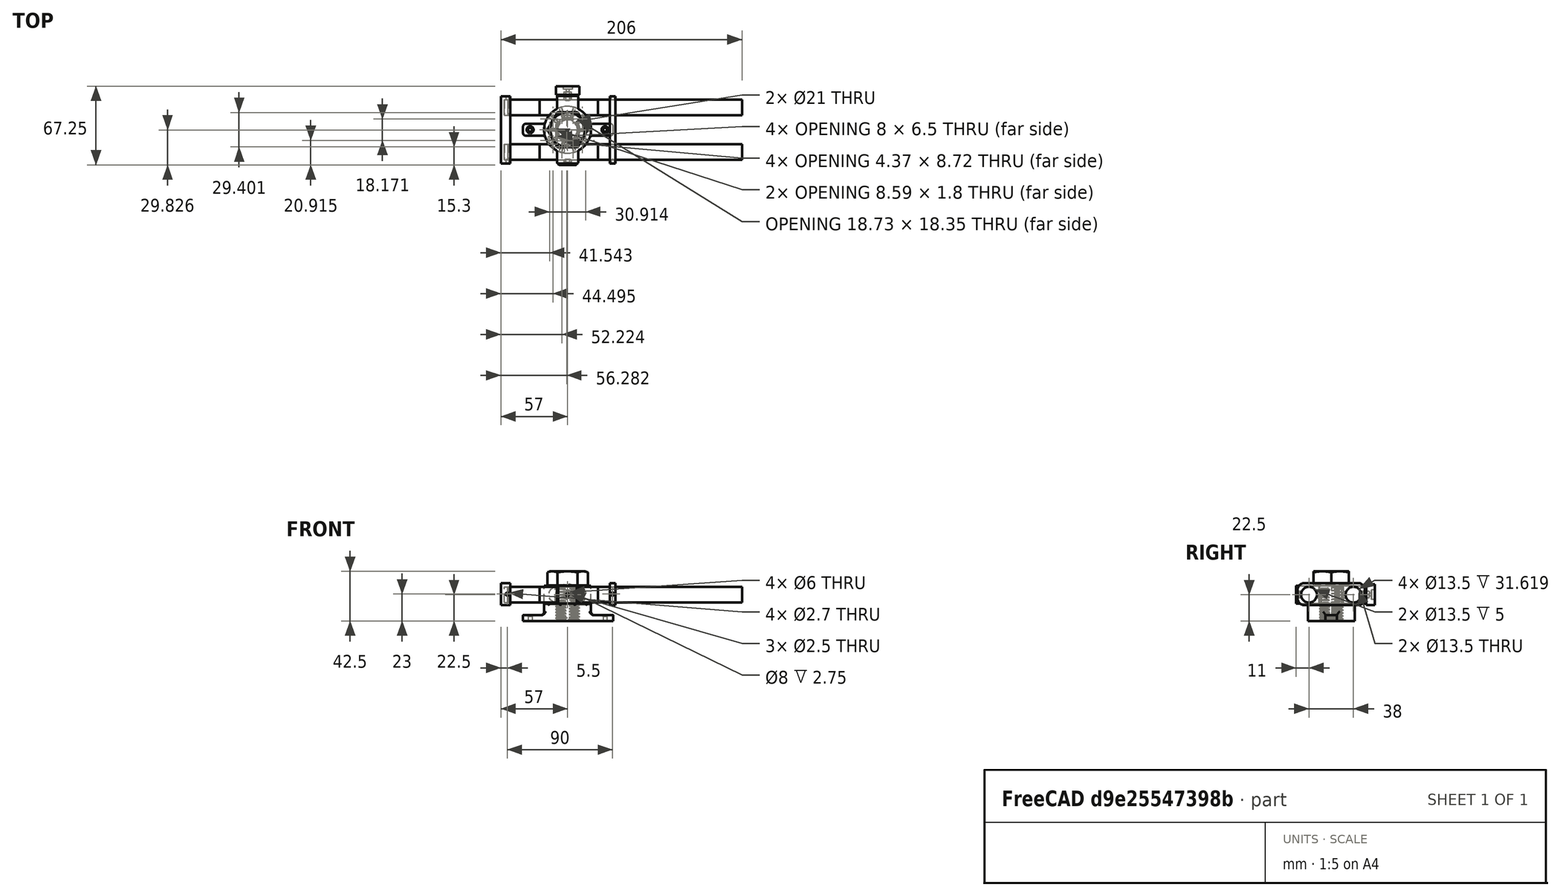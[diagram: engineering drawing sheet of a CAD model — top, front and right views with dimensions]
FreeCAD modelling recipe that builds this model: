
FCSTD DOCUMENT  (FreeCAD 0.18R4 (GitTag))
Label: soporte_microfono
License: All rights reserved
LicenseURL: http://en.wikipedia.org/wiki/All_rights_reserved
objects: Part::Cylinder×31, Part::Cut×25, Part::Box×11, Part::Fillet×11, Part::MultiFuse×9, Mesh::Feature×7, Part::FeaturePython×5, App::DocumentObjectGroup×4, Part::Prism×3, Sketcher::SketchObject×2, PartDesign::FeatureBase×2, PartDesign::Hole×2, PartDesign::Body×2, PartDesign::Mirrored×1, PartDesign::MultiTransform×1
note: 107 computed .brp shape members not serialized (recipe doc carries the construction recipe); baked Part::Feature solids carry a one-line shape summary decoded from their .brp

FEATURE [Part::Cylinder] Cylinder
  Angle = 360
  AttacherType = Attacher::AttachEngine3D
  Height = 15
  Radius = 20
FEATURE [Part::Cylinder] Cylinder001
  Angle = 360
  AttacherType = Attacher::AttachEngine3D
  Height = 22
  Placement = pos=(0,0,15) rot=(0,1,0;1.5708rad)
  Radius = 1.1
FEATURE [Part::FeaturePython] Array  # Draft array (typed FeaturePython)
  Angle = 360
  ArrayType = 1
  Axis = (0,0,1)
  Base = -> Cylinder001
  Center = (0,0,0)
  Fuse = false
  IntervalAxis = (0,0,0)
  IntervalX = (1,0,0)
  IntervalY = (0,1,0)
  IntervalZ = (0,0,1)
  NumberPolar = 10
  NumberX = 2
  NumberY = 2
  NumberZ = 1
FEATURE [Part::Cylinder] Cylinder002
  Angle = 360
  AttacherType = Attacher::AttachEngine3D
  Height = 19.75
  Placement = pos=(0,0,15) rot=(0,1,0;1.5708rad)
  Radius = 0.9
FEATURE [Part::FeaturePython] Array001  # Draft array (typed FeaturePython)
  Angle = 360
  ArrayType = 1
  Axis = (0,0,1)
  Base = -> Cylinder002
  Center = (0,0,0)
  Fuse = false
  IntervalAxis = (0,0,0)
  IntervalX = (1,0,0)
  IntervalY = (0,1,0)
  IntervalZ = (0,0,1)
  NumberPolar = 10
  NumberX = 2
  NumberY = 2
  NumberZ = 1
FEATURE [Part::Cylinder] Cylinder003
  Angle = 360
  AttacherType = Attacher::AttachEngine3D
  Height = 23
  Radius = 11
FEATURE [Part::Cylinder] Cylinder004
  Angle = 360
  AttacherType = Attacher::AttachEngine3D
  Height = 23
  Radius = 11.2
FEATURE [Part::Cut] Cut001
  Base = -> Array
  Refine = true
  Tool = -> Cylinder003
FEATURE [Part::Cut] Cut002  label="aspas"
  Base = -> Array001
  Refine = true
  Tool = -> Cylinder004
FEATURE [Part::Box] Box  label="Cube"
  AttacherType = Attacher::AttachEngine3D
  Height = 5
  Length = 25
  Placement = pos=(14,-5,0) rot=(0,0,1;0rad)
  Width = 10
FEATURE [Part::Box] Box001  label="Cube001"
  AttacherType = Attacher::AttachEngine3D
  Height = 5
  Length = 25
  Placement = pos=(-38,-5,0) rot=(0,0,1;0rad)
  Width = 10
FEATURE [Part::Cylinder] Cylinder005
  Angle = 360
  AttacherType = Attacher::AttachEngine3D
  Height = 15
  Placement = pos=(0,0,15) rot=(0,0,1;0rad)
  Radius = 20
FEATURE [Part::Cylinder] Cylinder006
  Angle = 360
  AttacherType = Attacher::AttachEngine3D
  Height = 32
  Radius = 10.5
FEATURE [Part::Cut] Cut004
  Base = -> Cylinder005
  Refine = true
  Tool = -> Cylinder006
FEATURE [Part::MultiFuse] Fusion001
  Refine = true
  Shapes = -> [Cut004,Cut002]
FEATURE [Part::Cylinder] Cylinder007
  Angle = 360
  AttacherType = Attacher::AttachEngine3D
  Height = 50
  Placement = pos=(-24,19,22.5) rot=(0,1,0;1.5708rad)
  Radius = 6.75
FEATURE [Part::Box] Box002  label="Cube002"
  AttacherType = Attacher::AttachEngine3D
  Height = 15
  Length = 18
  Placement = pos=(-9,-29,15) rot=(0,0,1;0rad)
  Width = 18
FEATURE [Part::Box] Box003  label="Cube003"
  AttacherType = Attacher::AttachEngine3D
  Height = 15
  Length = 18
  Placement = pos=(-9,11,15) rot=(0,0,1;0rad)
  Width = 18
FEATURE [Part::MultiFuse] Fusion002
  Refine = true
  Shapes = -> [Fusion001,Box002,Box003]
FEATURE [Part::Cylinder] Cylinder008
  Angle = 360
  AttacherType = Attacher::AttachEngine3D
  Height = 50
  Placement = pos=(-24,-19,22.5) rot=(0,1,0;1.5708rad)
  Radius = 6.75
FEATURE [Part::Cut] Cut005
  Base = -> Fusion002
  Refine = true
  Tool = -> Cylinder008
FEATURE [Part::Cut] Cut006
  Base = -> Cut005
  Refine = true
  Tool = -> Cylinder007
FEATURE [Part::Fillet] Fillet003  label="part_soporte_inferior_estante"
  Base = -> Cut006
  Edges = 12 edges r=1: [Edge2,Edge5,Edge7,Edge19,Edge21,Edge74,Edge75,Edge76,Edge77,Edge79,Edge80,Edge83]
FEATURE [Sketcher::SketchObject] Sketch002
  ExternalGeometry = -> [Fillet003]
  MapMode = 5
  Placement = pos=(0,0,0) rot=(1,0,0;1.5708rad)
  Support = -> [XZ_Plane001]
  sketch-geometry (1):
    g0: Circle CenterX=-1e-15 CenterY=22.5 CenterZ=0 NormalX=0 NormalY=0 NormalZ=1 AngleXU=0 Radius=1.25
  constraints (2):
    c: Radius(g0) = 1.25
    c: Symmetric(g-3,g-4,g0)
FEATURE [App::DocumentObjectGroup] Group  label="sketches"
  Group = -> [Sketch002]
FEATURE [PartDesign::FeatureBase] BaseFeature001
  BaseFeature = -> Fillet003
FEATURE [PartDesign::Hole] Hole001
  BaseFeature = -> BaseFeature001
  Depth = 25
  DepthType = 1
  Diameter = 6
  DrillPoint = 1
  DrillPointAngle = 118
  HoleCutCountersinkAngle = 90
  HoleCutDepth = 0
  HoleCutDiameter = 0
  HoleCutType = 0
  ModelActualThread = false
  Profile = -> Sketch002
  Refine = true
  Tapered = false
  TaperedAngle = 90
  ThreadAngle = 0
  ThreadClass = 0
  ThreadCutOffInner = 0
  ThreadCutOffOuter = 0
  ThreadDirection = 0
  ThreadFit = 0
  ThreadPitch = 0
  ThreadSize = 0
  ThreadType = 0
  Threaded = false
FEATURE [PartDesign::Mirrored] Mirrored
  MirrorPlane = -> XZ_Plane001
  Refine = true
FEATURE [PartDesign::MultiTransform] MultiTransform
  BaseFeature = -> Hole001
  Originals = -> [Hole001]
  Refine = true
  Transformations = -> [Mirrored]
FEATURE [PartDesign::Body] Body001  label="final_soporte_inferior_estante"
  BaseFeature = -> Fillet003
  Group = -> [BaseFeature001,Sketch002,Hole001,MultiTransform,Mirrored]
  Origin = -> Origin001
  Tip = -> MultiTransform
FEATURE [Part::Cylinder] Cylinder009  label="tubo_base"
  Angle = 360
  AttacherType = Attacher::AttachEngine3D
  Height = 50
  Placement = pos=(-24,19,22.5) rot=(0,1,0;1.5708rad)
  Radius = 6.75
FEATURE [Part::FeaturePython] Screw  label="final_tornillo_soportes_estante"  # Fasteners workbench fastener (typed FeaturePython)
  Placement = pos=(0,0,30) rot=(0,0,1;0rad)
  baseObject = -> Body001 [Edge24]
  diameter = 15
  invert = false
  length = 15
  lengthCustom = 29
  matchOuter = false
  offset = 0
  thread = true
  type = 27
FEATURE [Part::FeaturePython] ScrewTap  label="M20x40.0-ScrewTap"  # Fasteners workbench fastener (typed FeaturePython)
  Placement = pos=(0,0,15) rot=(0,0,1;0rad)
  baseObject = -> Cylinder [Edge1]
  diameter = 14
  invert = false
  length = 40
  matchOuter = false
  offset = 0
  thread = true
FEATURE [Part::Cut] Cut
  Base = -> Cylinder
  Refine = true
  Tool = -> ScrewTap
FEATURE [Part::Cut] Cut003
  Base = -> Cut
  Refine = true
  Tool = -> Cut001
FEATURE [Part::MultiFuse] Fusion
  Refine = true
  Shapes = -> [Box001,Box,Cut003]
FEATURE [Part::Fillet] Fillet
  Base = -> Fusion
  Edges = 7 edges r=3: [Edge6,Edge9,Edge11,Edge42,Edge43,Edge46,Edge47]
FEATURE [Part::Fillet] Fillet001
  Base = -> Fillet
  Edges = 1 edges r=2: [Edge24]
FEATURE [Part::Fillet] Fillet002  label="final_part_soporte_superior_estante"
  Base = -> Fillet001
  Edges = 3 edges r=2: [Edge27,Edge71,Edge74]
FEATURE [PartDesign::FeatureBase] BaseFeature
  BaseFeature = -> Fillet002
FEATURE [Sketcher::SketchObject] Sketch
  MapMode = 5
  Placement = pos=(0,0,5) rot=(0,0,1;0rad)
  Support = -> [BaseFeature]
  sketch-geometry (2):
    g0: Circle CenterX=-32 CenterY=0 CenterZ=0 NormalX=0 NormalY=0 NormalZ=1 AngleXU=0 Radius=0.5
    g1: Circle CenterX=32 CenterY=0 CenterZ=0 NormalX=0 NormalY=0 NormalZ=1 AngleXU=0 Radius=0.5
  constraints (5):
    c: PointOnObject(g0,g-1)
    c: Symmetric(g0,g1,g-2)
    c: Radius(g0) = 0.5
    c: Equal(g0,g1)
    c: DistanceX(g0,g-1) = 32
FEATURE [PartDesign::Hole] Hole
  BaseFeature = -> BaseFeature
  Depth = 25
  DepthType = 1
  Diameter = 3.3
  DrillPoint = 1
  DrillPointAngle = 118
  HoleCutCountersinkAngle = 90
  HoleCutDepth = 0
  HoleCutDiameter = 6
  HoleCutType = 2
  ModelActualThread = false
  Profile = -> Sketch
  Refine = true
  Tapered = false
  TaperedAngle = 90
  ThreadAngle = 0
  ThreadClass = 0
  ThreadCutOffInner = 0
  ThreadCutOffOuter = 0
  ThreadDirection = 0
  ThreadFit = 0
  ThreadPitch = 0
  ThreadSize = 3
  ThreadType = 1
  Threaded = false
FEATURE [PartDesign::Body] Body  label="soporte_superior_estante_1"
  BaseFeature = -> Fillet002
  Group = -> [BaseFeature,Sketch,Hole]
  Origin = -> Origin
  Tip = -> Hole
FEATURE [Part::Cylinder] Cylinder010  label="Cylinder009"
  Angle = 360
  AttacherType = Attacher::AttachEngine3D
  Height = 15
  Radius = 11
FEATURE [Part::MultiFuse] Fusion003
  Refine = true
  Shapes = -> [Body,Cylinder010]
FEATURE [Part::FeaturePython] ScrewTap001  label="M20x40.0-ScrewTap001"  # Fasteners workbench fastener (typed FeaturePython)
  Placement = pos=(0,0,28.5) rot=(0,0,1;0rad)
  baseObject = -> Fusion003 [Edge143]
  diameter = 14
  invert = false
  length = 40
  matchOuter = false
  offset = 13.5
  thread = true
FEATURE [Part::Cut] Cut007  label="final_soporte_superior_estante"
  Base = -> Fusion003
  Refine = true
  Tool = -> ScrewTap001
FEATURE [Mesh::Feature] Mesh001  label="tornillo_soportes_estante (Meshed)"
FEATURE [Mesh::Feature] Mesh002  label="final_soporte_superior_estante (Meshed)"
FEATURE [Part::Cylinder] Cylinder011  label="Cylinder010"
  Angle = 360
  AttacherType = Attacher::AttachEngine3D
  Height = 50
  Placement = pos=(0,-16,22.5) rot=(1,0,0;1.5708rad)
  Radius = 1.25
FEATURE [Part::Cylinder] Cylinder012  label="Cylinder011"
  Angle = 360
  AttacherType = Attacher::AttachEngine3D
  Height = 50
  Placement = pos=(0,69,22.5) rot=(1,0,0;1.5708rad)
  Radius = 1.25
FEATURE [Part::Cut] Cut008
  Base = -> Fillet003
  Refine = true
  Tool = -> Cylinder011
FEATURE [Part::Cut] Cut009
  Base = -> Cut008
  Refine = true
  Tool = -> Cylinder012
FEATURE [Part::Prism] Prism
  AttacherType = Attacher::AttachEngine3D
  Circumradius = 3.15
  Height = 2.4
  Placement = pos=(0,28,22.5) rot=(1,0,0;1.5708rad)
  Polygon = 6
FEATURE [Part::Prism] Prism001
  AttacherType = Attacher::AttachEngine3D
  Circumradius = 3.15
  Height = 2.4
  Placement = pos=(0,-25.5,22.5) rot=(1,0,0;1.5708rad)
  Polygon = 6
FEATURE [Mesh::Feature] Mesh003  label="final_soporte_inferior_estante1 (Meshed)"
FEATURE [Part::Cylinder] Cylinder013  label="Cylinder012"
  Angle = 360
  AttacherType = Attacher::AttachEngine3D
  Height = 50
  Placement = pos=(0,-16,22.5) rot=(1,0,0;1.5708rad)
  Radius = 1.25
FEATURE [Part::Prism] Prism002
  AttacherType = Attacher::AttachEngine3D
  Circumradius = 3.15
  Height = 2.5
  Placement = pos=(0,29,22.5) rot=(1,0,0;1.5708rad)
  Polygon = 6
FEATURE [Part::Cylinder] Cylinder014  label="Cylinder013"
  Angle = 360
  AttacherType = Attacher::AttachEngine3D
  Height = 10
  Placement = pos=(0,-16,22.5) rot=(1,0,0;1.5708rad)
  Radius = 4
FEATURE [Part::MultiFuse] Fusion004
  Placement = pos=(0,57,0) rot=(0,0,1;0rad)
  Refine = true
  Shapes = -> [Cylinder013,Cylinder014]
FEATURE [Part::MultiFuse] Fusion005
  Placement = pos=(0,-26.5,-5) rot=(0,0,1;0rad)
  Refine = true
  Shapes = -> [Prism002,Fusion004]
FEATURE [Part::Box] Box004  label="Cube004"
  AttacherType = Attacher::AttachEngine3D
  Height = 10
  Length = 20
  Placement = pos=(-10,0,12.5) rot=(0,0,1;0rad)
  Width = 7.25
FEATURE [Part::Cut] Cut012
  Base = -> Box004
  Refine = true
  Tool = -> Fusion005
FEATURE [Part::Cylinder] Cylinder015  label="Cylinder014"
  Angle = 360
  AttacherType = Attacher::AttachEngine3D
  Height = 7.25
  Placement = pos=(0,0,17.5) rot=(1,0,0;1.5708rad)
  Radius = 9
FEATURE [Part::Cylinder] Cylinder016  label="Cylinder015"
  Angle = 360
  AttacherType = Attacher::AttachEngine3D
  Height = 7.25
  Placement = pos=(0,0,17.5) rot=(1,0,0;1.5708rad)
  Radius = 4
FEATURE [Part::Cut] Cut013
  Base = -> Cylinder015
  Placement = pos=(0,7.25,0) rot=(0,0,1;0rad)
  Refine = true
  Tool = -> Cylinder016
FEATURE [Part::Fillet] Fillet004
  Base = -> Cut012
  Edges = 1 edges r=3: [Edge15]
FEATURE [Part::Fillet] Fillet005
  Base = -> Fillet004
  Edges = 3 edges r=3: [Edge13,Edge17,Edge20]
FEATURE [Part::MultiFuse] Fusion006
  Refine = true
  Shapes = -> [Cut013,Fillet005]
FEATURE [Part::Fillet] Fillet006  label="tornillos_para_metal"
  Base = -> Fusion006
  Edges = 4 edges r=1: [Edge5,Edge9,Edge12,Edge17]
  Placement = pos=(0,30,5) rot=(0,0,1;0rad)
FEATURE [Mesh::Feature] Mesh004  label="tornillos_para_metal (Meshed)"
FEATURE [Part::Cylinder] Cylinder017  label="tubo1"
  Angle = 360
  AttacherType = Attacher::AttachEngine3D
  Height = 50
  Placement = pos=(-24,-19,22.5) rot=(0,1,0;1.5708rad)
  Radius = 6.75
FEATURE [Part::Cylinder] Cylinder018  label="tubo2"
  Angle = 360
  AttacherType = Attacher::AttachEngine3D
  Height = 50
  Placement = pos=(-24,19,22.5) rot=(0,1,0;1.5708rad)
  Radius = 6.75
FEATURE [Part::Cylinder] Cylinder019  label="tubo003"
  Angle = 360
  AttacherType = Attacher::AttachEngine3D
  Height = 50
  Placement = pos=(-24,-19,22.5) rot=(0,1,0;1.5708rad)
  Radius = 6.75
FEATURE [Part::Cylinder] Cylinder020  label="tubo004"
  Angle = 360
  AttacherType = Attacher::AttachEngine3D
  Height = 50
  Placement = pos=(-24,19,22.5) rot=(0,1,0;1.5708rad)
  Radius = 6.75
FEATURE [Part::Box] Box005  label="Cube005"
  AttacherType = Attacher::AttachEngine3D
  Height = 19
  Length = 5
  Placement = pos=(0,-28.75,13.5) rot=(0,0,1;0rad)
  Width = 57.5
FEATURE [Part::Fillet] Fillet007
  Base = -> Box005
  Edges = 4 edges r=6: [Edge9,Edge10,Edge11,Edge12]
FEATURE [Part::Cylinder] Cylinder021  label="Cylinder016"
  Angle = 360
  AttacherType = Attacher::AttachEngine3D
  Height = 10
  Placement = pos=(2.5,32,23) rot=(1,0,0;1.5708rad)
  Radius = 1.35
FEATURE [Part::Cut] Cut016
  Base = -> Fillet007
  Refine = true
  Tool = -> Cylinder019
FEATURE [Part::Cut] Cut017
  Base = -> Cut016
  Refine = true
  Tool = -> Cylinder020
FEATURE [Part::Cylinder] Cylinder022  label="Cylinder017"
  Angle = 360
  AttacherType = Attacher::AttachEngine3D
  Height = 10
  Placement = pos=(2.5,-22,23) rot=(1,0,0;1.5708rad)
  Radius = 1.35
FEATURE [Part::Cut] Cut018
  Base = -> Cut017
  Refine = true
  Tool = -> Cylinder021
FEATURE [Part::Cut] Cut019  label="soporte_separador_tubos"
  Base = -> Cut018
  Placement = pos=(36,0,0) rot=(0,0,1;0rad)
  Refine = true
  Tool = -> Cylinder022
FEATURE [Part::Box] Box006  label="Cube006"
  AttacherType = Attacher::AttachEngine3D
  Height = 19
  Length = 5
  Placement = pos=(0,-28.75,13.5) rot=(0,0,1;0rad)
  Width = 57.5
FEATURE [Part::Fillet] Fillet008
  Base = -> Box006
  Edges = 4 edges r=6: [Edge9,Edge10,Edge11,Edge12]
  Placement = pos=(-24,0,0) rot=(0,0,1;0rad)
FEATURE [Part::Cylinder] Cylinder023  label="tubo005"
  Angle = 360
  AttacherType = Attacher::AttachEngine3D
  Height = 200
  Placement = pos=(-51,-19,22.5) rot=(0,1,0;1.5708rad)
  Radius = 6.75
FEATURE [Part::Cylinder] Cylinder024  label="tubo006"
  Angle = 360
  AttacherType = Attacher::AttachEngine3D
  Height = 200
  Placement = pos=(-51,19,22.5) rot=(0,1,0;1.5708rad)
  Radius = 6.75
FEATURE [Part::Box] Box007  label="Cube007"
  AttacherType = Attacher::AttachEngine3D
  Height = 19
  Length = 5
  Placement = pos=(0,-28.75,13.5) rot=(0,0,1;0rad)
  Width = 57.5
FEATURE [Part::Fillet] Fillet009
  Base = -> Box007
  Edges = 4 edges r=6: [Edge9,Edge10,Edge11,Edge12]
FEATURE [Part::Cylinder] Cylinder025  label="Cylinder018"
  Angle = 360
  AttacherType = Attacher::AttachEngine3D
  Height = 10
  Placement = pos=(2.5,32,23) rot=(1,0,0;1.5708rad)
  Radius = 1.35
FEATURE [Part::Cylinder] Cylinder026  label="tubo007"
  Angle = 360
  AttacherType = Attacher::AttachEngine3D
  Height = 50
  Placement = pos=(-24,-19,22.5) rot=(0,1,0;1.5708rad)
  Radius = 6.75
FEATURE [Part::Cylinder] Cylinder027  label="Cylinder019"
  Angle = 360
  AttacherType = Attacher::AttachEngine3D
  Height = 10
  Placement = pos=(2.5,-22,23) rot=(1,0,0;1.5708rad)
  Radius = 1.35
FEATURE [Part::Cylinder] Cylinder028  label="tubo008"
  Angle = 360
  AttacherType = Attacher::AttachEngine3D
  Height = 50
  Placement = pos=(-24,19,22.5) rot=(0,1,0;1.5708rad)
  Radius = 6.75
FEATURE [Part::Cut] Cut022
  Base = -> Fillet009
  Refine = true
  Tool = -> Cylinder026
FEATURE [Part::Cut] Cut020
  Base = -> Cut022
  Refine = true
  Tool = -> Cylinder028
FEATURE [Part::Cut] Cut023
  Base = -> Cut020
  Refine = true
  Tool = -> Cylinder025
FEATURE [Part::Cut] Cut021  label="soporte_tubos001"
  Base = -> Cut023
  Refine = true
  Tool = -> Cylinder027
FEATURE [Part::Box] Box008  label="Cube008"
  AttacherType = Attacher::AttachEngine3D
  Height = 42
  Length = 10
  Placement = pos=(-32,-32,0) rot=(0,0,1;0rad)
  Width = 64
FEATURE [Part::Cut] Cut024
  Base = -> Fillet008
  Placement = pos=(19,0,0) rot=(0,0,1;0rad)
  Refine = true
  Tool = -> Box008
FEATURE [Part::MultiFuse] Fusion007  label="soporte_tapa_tubos"
  Placement = pos=(-54,0,0) rot=(0,0,1;0rad)
  Refine = true
  Shapes = -> [Cut021,Cut024]
FEATURE [Part::Cut] Cut025
  Base = -> Cut009
  Refine = true
  Tool = -> Prism001
FEATURE [Part::Cut] Cut026  label="final_soporte_inferior_estante11"
  Base = -> Cut025
  Refine = true
  Tool = -> Prism
FEATURE [Part::Cylinder] Cylinder029  label="Cylinder020"
  Angle = 360
  AttacherType = Attacher::AttachEngine3D
  Height = 50
  Placement = pos=(0,69,22.5) rot=(1,0,0;1.5708rad)
  Radius = 1.25
FEATURE [Part::Box] Box009  label="Cube009"
  AttacherType = Attacher::AttachEngine3D
  Height = 15
  Length = 16
  Placement = pos=(-8,29,15) rot=(0,0,1;0rad)
  Width = 1
FEATURE [Part::Cut] Cut027
  Base = -> Box009
  Refine = true
  Tool = -> Cylinder029
FEATURE [Part::Box] Box010  label="Cube010"
  AttacherType = Attacher::AttachEngine3D
  Height = 15
  Length = 16
  Placement = pos=(-8,29,15) rot=(0,0,1;0rad)
  Width = 1
FEATURE [Part::Cylinder] Cylinder030  label="Cylinder021"
  Angle = 360
  AttacherType = Attacher::AttachEngine3D
  Height = 50
  Placement = pos=(0,69,22.5) rot=(1,0,0;1.5708rad)
  Radius = 1.25
FEATURE [Part::Cut] Cut028
  Base = -> Box010
  Placement = pos=(0,-59,0) rot=(0,0,1;0rad)
  Refine = true
  Tool = -> Cylinder030
FEATURE [Part::MultiFuse] Fusion008
  Refine = true
  Shapes = -> [Cut028,Cut026,Cut027]
FEATURE [Part::Fillet] Fillet010  label="final_soporte_inferior_estante1"
  Base = -> Fusion008
  Edges = 4 edges r=0.9: [Edge1,Edge6,Edge99,Edge102]
FEATURE [Mesh::Feature] Mesh007  label="final_soporte_inferior_estante1 (Meshed)001"
FEATURE [App::DocumentObjectGroup] Group001  label="final_piezas_originales"
  Group = -> [Fillet002,Cylinder023,Cylinder024,Fillet010,Screw,Fillet006,Cut019,Fusion007]
FEATURE [App::DocumentObjectGroup] Group003  label="old"
  Group = -> [Body001,Cut007]
FEATURE [Mesh::Feature] Mesh  label="soporte_separador_tubos (Meshed)"
FEATURE [Mesh::Feature] Mesh008  label="soporte_tapa_tubos (Meshed)"
FEATURE [App::DocumentObjectGroup] Group002  label="final_meshed"
  Group = -> [Mesh007,Mesh004,Mesh001,Mesh002,Mesh003,Mesh,Mesh008]
